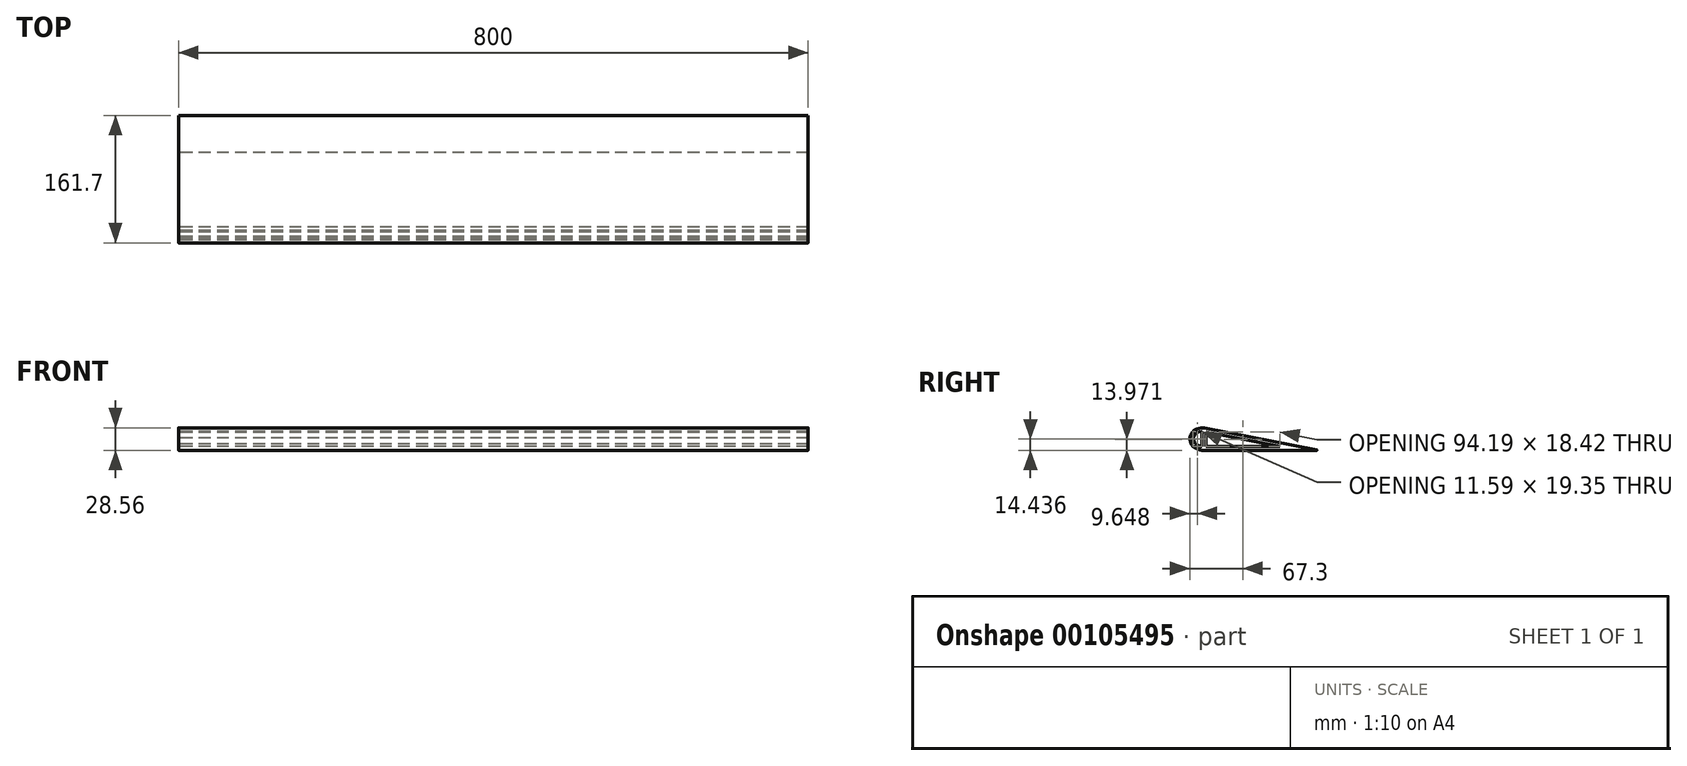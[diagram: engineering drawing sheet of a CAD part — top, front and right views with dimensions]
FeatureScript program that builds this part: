
annotation { "Feature Type Name" : "Feature", "Feature Type Description" : "" }
export const myFeature = defineFeature(function(context is Context, id is Id, definition is map)
    precondition{}
    {
        {
            var Q0;
            Q0=qCreatedBy(makeId("Right.planeOp"),FACE);
            var sketch = newSketch(context, id + "F0", { "sketchPlane" : qUnion([Q0])});
            skLineSegment(sketch, "E0", {"start": v(0, 0) * mm, "end": v(150, 0) * mm});
            skLineSegment(sketch, "E1", {"start": v(150, 0) * mm, "end": v(2.79, 28.78) * mm});
            skLineSegment(sketch, "E2", {"start": v(2.79, 28.78) * mm, "end": v(1.87, 24.11) * mm});
            skLineSegment(sketch, "E3", {"start": v(1.87, 24.11) * mm, "end": v(125.18, 0) * mm});
            skLineSegment(sketch, "E4", {"start": v(0, 0) * mm, "end": v(0, 4.76) * mm});
            skLineSegment(sketch, "E5", {"start": v(0, 4.76) * mm, "end": v(100.82, 4.76) * mm});
            skLineSegment(sketch, "E6", {"start": v(0, 0) * mm, "end": v(-10.76, 4.76) * mm});
            skLineSegment(sketch, "E7", {"start": v(-10.76, 4.76) * mm, "end": v(-14.46, 15.93) * mm});
            skLineSegment(sketch, "E8", {"start": v(-14.46, 15.93) * mm, "end": v(-8.68, 26.17) * mm});
            skLineSegment(sketch, "E9", {"start": v(-8.68, 26.17) * mm, "end": v(2.79, 28.78) * mm});
            skLineSegment(sketch, "E10", {"start": v(-8.68, 26.17) * mm, "end": v(-5.84, 22.36) * mm});
            skLineSegment(sketch, "E11", {"start": v(-10.76, 4.76) * mm, "end": v(-7.23, 7.96) * mm});
            skLineSegment(sketch, "E12", {"start": v(-14.46, 15.93) * mm, "end": v(-9.72, 15.47) * mm});
            skLineSegment(sketch, "E13", {"start": v(1.87, 24.11) * mm, "end": v(-5.84, 22.36) * mm});
            skLineSegment(sketch, "E14", {"start": v(-5.84, 22.36) * mm, "end": v(-9.72, 15.47) * mm});
            skLineSegment(sketch, "E15", {"start": v(-9.72, 15.47) * mm, "end": v(-7.23, 7.96) * mm});
            skLineSegment(sketch, "E16", {"start": v(-7.23, 7.96) * mm, "end": v(0, 4.76) * mm});
            skLineSegment(sketch, "E17", {"start": v(1.87, 24.11) * mm, "end": v(1.87, 4.76) * mm});
            skLineSegment(sketch, "E18", {"start": v(6.64, 4.76) * mm, "end": v(6.64, 23.18) * mm});
            skSolve(sketch);
        }
        {
            var Q0;
            {var subQ3=sQuery(id+"F0.wireOp",EDGE,"E1");Q0=makeQuery(id+"F0.imprint","IMPRINT",FACE,{"disambiguationData":[TD([[makeQuery(id+"F0.imprint","IMPRINT",EDGE,{"derivedFrom":subQ3}),1.0]])]});}
            var Q1;
            {var subQ1=sQuery(id+"F0.wireOp",EDGE,"E4");Q1=makeQuery(id+"F0.imprint","IMPRINT",FACE,{"disambiguationData":[TD([[makeQuery(id+"F0.imprint","IMPRINT",EDGE,{"derivedFrom":subQ1}),-1.0]])]});}
            var Q2;
            {var subQ0=sQuery(id+"F0.wireOp",EDGE,"E17");Q2=makeQuery(id+"F0.imprint","IMPRINT",FACE,{"disambiguationData":[TD([[makeQuery(id+"F0.imprint","IMPRINT",EDGE,{"derivedFrom":subQ0}),1.0]])]});}
            var Q3;
            Q3=makeQuery(id+"F0.imprint","IMPRINT",FACE,{"disambiguationData":[TD([[makeQuery(id+"F0.imprint","IMPRINT",EDGE,{"derivedFrom":sQuery(id+"F0.wireOp",EDGE,"E2")}),-1.0]])]});
            var Q4;
            Q4=makeQuery(id+"F0.imprint","IMPRINT",FACE,{"disambiguationData":[TD([[makeQuery(id+"F0.imprint","IMPRINT",EDGE,{"derivedFrom":sQuery(id+"F0.wireOp",EDGE,"E4")}),1.0]])]});
            var Q5;
            Q5=makeQuery(id+"F0.imprint","IMPRINT",FACE,{"disambiguationData":[TD([[makeQuery(id+"F0.imprint","IMPRINT",EDGE,{"derivedFrom":sQuery(id+"F0.wireOp",EDGE,"E7")}),-1.0]])]});
            var Q6;
            Q6=makeQuery(id+"F0.imprint","IMPRINT",FACE,{"disambiguationData":[TD([[makeQuery(id+"F0.imprint","IMPRINT",EDGE,{"derivedFrom":sQuery(id+"F0.wireOp",EDGE,"E8")}),-1.0]])]});
            extrude(context, id + "F1", {"entities" : qUnion([Q0, Q1, Q2, Q3, Q4, Q5, Q6]), "depth" : 800 * mm});
        }
        {
            var Q0;
            Q0=makeQuery(id+"F1.opExtrude","SWEPT_EDGE",EDGE,{"disambiguationData":[OSD([sQuery(id+"F0.wireOp",EDGE,"E8"),sQuery(id+"F0.wireOp",EDGE,"E9"),sQuery(id+"F0.wireOp",EDGE,"E10")])]});
            var Q1;
            Q1=makeQuery(id+"F1.opExtrude","SWEPT_EDGE",EDGE,{"disambiguationData":[OSD([sQuery(id+"F0.wireOp",EDGE,"E7"),sQuery(id+"F0.wireOp",EDGE,"E8"),sQuery(id+"F0.wireOp",EDGE,"E12")])]});
            var Q2;
            Q2=makeQuery(id+"F1.opExtrude","SWEPT_EDGE",EDGE,{"disambiguationData":[OSD([sQuery(id+"F0.wireOp",EDGE,"E1"),sQuery(id+"F0.wireOp",EDGE,"E2"),sQuery(id+"F0.wireOp",EDGE,"E9")])]});
            var Q3;
            Q3=makeQuery(id+"F1.opExtrude","SWEPT_EDGE",EDGE,{"disambiguationData":[OSD([sQuery(id+"F0.wireOp",EDGE,"E6"),sQuery(id+"F0.wireOp",EDGE,"E7"),sQuery(id+"F0.wireOp",EDGE,"E11")])]});
            var Q4;
            Q4=makeQuery(id+"F1.opExtrude","SWEPT_EDGE",EDGE,{"disambiguationData":[OSD([sQuery(id+"F0.wireOp",EDGE,"E0"),sQuery(id+"F0.wireOp",EDGE,"E4"),sQuery(id+"F0.wireOp",EDGE,"E6")])]});
            fillet(context, id + "F2", {"entities" : qUnion([Q0, Q1, Q2, Q3, Q4]), "radius" : 10 * mm, "tangentPropagation" : true, "allowEdgeOverflow" : false});
        }
        {
            var Q0;
            Q0=makeQuery(id+"F1.opExtrude","SWEPT_EDGE",EDGE,{"disambiguationData":[OSD([sQuery(id+"F0.wireOp",EDGE,"E0"),sQuery(id+"F0.wireOp",EDGE,"E1")])]});
            fillet(context, id + "F3", {"entities" : qUnion([Q0]), "radius" : 0.2 * mm, "tangentPropagation" : true, "allowEdgeOverflow" : false});
        }
    });
